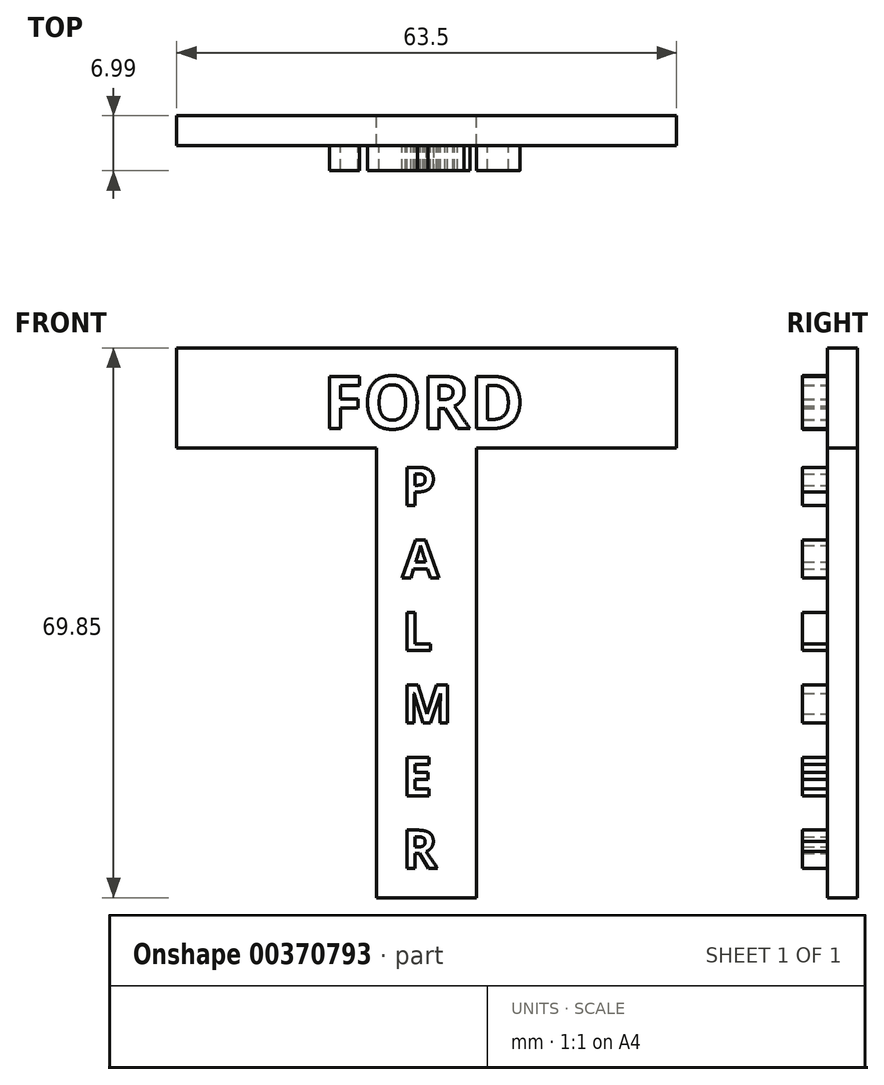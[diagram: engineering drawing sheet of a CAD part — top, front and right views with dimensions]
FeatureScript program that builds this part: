
annotation { "Feature Type Name" : "Feature", "Feature Type Description" : "" }
export const myFeature = defineFeature(function(context is Context, id is Id, definition is map)
    precondition{}
    {
        {
            var Q0;
            Q0=qCreatedBy(makeId("Front.planeOp"),FACE);
            var sketch = newSketch(context, id + "F0", { "sketchPlane" : qUnion([Q0])});
            skLineSegment(sketch, "E0", {"start": v(-16.66, -35.36) * mm, "end": v(-3.96, -35.36) * mm});
            skLineSegment(sketch, "E1", {"start": v(-3.96, -35.36) * mm, "end": v(-3.96, 21.8) * mm});
            skLineSegment(sketch, "E2", {"start": v(-3.96, 21.8) * mm, "end": v(21.44, 21.8) * mm});
            skLineSegment(sketch, "E3", {"start": v(21.44, 21.8) * mm, "end": v(21.44, 34.5) * mm});
            skLineSegment(sketch, "E4", {"start": v(21.44, 34.5) * mm, "end": v(-42.06, 34.5) * mm});
            skLineSegment(sketch, "E5", {"start": v(-42.06, 34.5) * mm, "end": v(-42.06, 21.8) * mm});
            skLineSegment(sketch, "E6", {"start": v(-42.06, 21.8) * mm, "end": v(-16.66, 21.8) * mm});
            skLineSegment(sketch, "E7", {"start": v(-16.66, 21.8) * mm, "end": v(-16.66, -35.36) * mm});
            skSolve(sketch);
        }
        {
            var Q0;
            Q0=makeQuery(id+"F0.imprint","IMPRINT",FACE,{"disambiguationData":[TD([[makeQuery(id+"F0.imprint","IMPRINT",EDGE,{"derivedFrom":sQuery(id+"F0.wireOp",EDGE,"E0")}),1.0]])]});
            extrude(context, id + "F1", {"entities" : qUnion([Q0]), "depth" : 3.8 * mm});
        }
        {
            var Q0;
            Q0=makeQuery(id+"F1.opExtrude","CAP_FACE",FACE,{"disambiguationData":[OSD([sQuery(id+"F0.wireOp",EDGE,"E0"),sQuery(id+"F0.wireOp",EDGE,"E1"),sQuery(id+"F0.wireOp",EDGE,"E2"),sQuery(id+"F0.wireOp",EDGE,"E3"),sQuery(id+"F0.wireOp",EDGE,"E4"),sQuery(id+"F0.wireOp",EDGE,"E5"),sQuery(id+"F0.wireOp",EDGE,"E6"),sQuery(id+"F0.wireOp",EDGE,"E7")])],"isStart":false});
            var sketch = newSketch(context, id + "F2", { "sketchPlane" : qUnion([Q0])});
            skText(sketch, "E8", { "text": "P\nA\nL\nM\nE\nR", "fontName": "OpenSans-Bold.ttf"});
            skText(sketch, "E9", { "text": "FORD", "fontName": "OpenSans-Bold.ttf"});
            const initialGuessF2  = {"E8": [-0.01341, 0.01448, 1, 0, 0.00488], "E9": [-0.02347, 0.02423, 1, 0, 0.0067]};
            skSetInitialGuess(sketch, initialGuessF2);
            skSolve(sketch);
        }
        {
            var Q0;
            Q0=makeQuery(id+"F1.opExtrude","CAP_FACE",FACE,{"disambiguationData":[OSD([sQuery(id+"F0.wireOp",EDGE,"E0"),sQuery(id+"F0.wireOp",EDGE,"E1"),sQuery(id+"F0.wireOp",EDGE,"E2"),sQuery(id+"F0.wireOp",EDGE,"E3"),sQuery(id+"F0.wireOp",EDGE,"E4"),sQuery(id+"F0.wireOp",EDGE,"E5"),sQuery(id+"F0.wireOp",EDGE,"E6"),sQuery(id+"F0.wireOp",EDGE,"E7")])],"isStart":false});
            var sketch = newSketch(context, id + "F3", { "sketchPlane" : qUnion([Q0])});
            skLineSegment(sketch, "E10", {"start": v(18.04, -21.91) * mm, "end": v(18.04, -34.61) * mm});
            skLineSegment(sketch, "E11", {"start": v(18.04, -34.61) * mm, "end": v(5.34, -34.61) * mm});
            skLineSegment(sketch, "E12", {"start": v(5.34, -34.61) * mm, "end": v(5.34, -21.91) * mm});
            skLineSegment(sketch, "E13", {"start": v(5.34, -21.91) * mm, "end": v(18.04, -21.91) * mm});
            skSolve(sketch);
        }
        {
            var Q0;
            Q0=makeQuery(id+"F3.imprint","IMPRINT",FACE,{"disambiguationData":[TD([[makeQuery(id+"F3.imprint","IMPRINT",EDGE,{"derivedFrom":sQuery(id+"F3.wireOp",EDGE,"E10")}),-1.0]])]});
            extrude(context, id + "F4", {"entities" : qUnion([Q0]), "depth" : 25.4 * mm});
        }
        {
            var Q0;
            Q0=makeQuery(id+"F4.opExtrude","SWEPT_BODY",BODY,{"disambiguationData":[OSD([sQuery(id+"F3.wireOp",EDGE,"E10"),sQuery(id+"F3.wireOp",EDGE,"E11"),sQuery(id+"F3.wireOp",EDGE,"E12"),sQuery(id+"F3.wireOp",EDGE,"E13")])]});
            deleteBodies(context, id + "F5", {"entities" : qUnion([Q0])});
        }
        {
            var Q0;
            Q0 = qSketchRegion(id + "F2", true);
            extrude(context, id + "F6", {"entities" : qUnion([Q0]), "operationType" : NewBodyOperationType.ADD, "depth" : 3.17 * mm});
        }
    });
